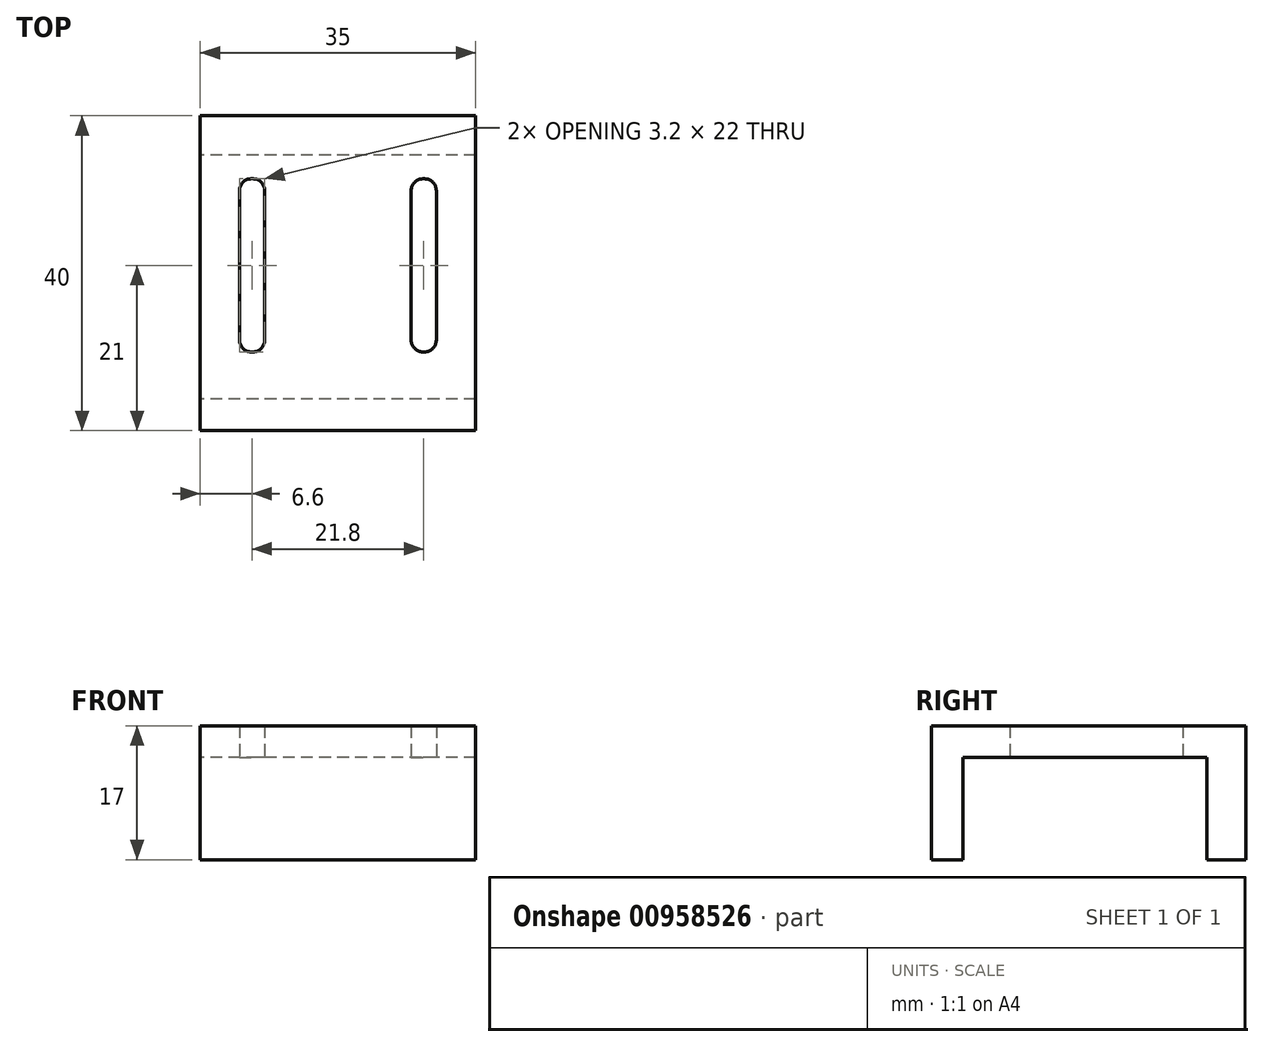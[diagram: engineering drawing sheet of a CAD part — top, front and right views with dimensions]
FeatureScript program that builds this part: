
annotation { "Feature Type Name" : "Feature", "Feature Type Description" : "" }
export const myFeature = defineFeature(function(context is Context, id is Id, definition is map)
    precondition{}
    {
        {
            var Q0;
            Q0=qCreatedBy(makeId("Top.planeOp"),FACE);
            var sketch = newSketch(context, id + "F0", { "sketchPlane" : qUnion([Q0])});
            skLineSegment(sketch, "E0.bottom", {"start": v(17.5, -20) * mm, "end": v(-17.5, -20) * mm});
            skLineSegment(sketch, "E0.top", {"start": v(17.5, 20) * mm, "end": v(-17.5, 20) * mm});
            skLineSegment(sketch, "E0.left", {"start": v(17.5, -20) * mm, "end": v(17.5, 20) * mm});
            skLineSegment(sketch, "E0.right", {"start": v(-17.5, -20) * mm, "end": v(-17.5, 20) * mm});
            skPoint(sketch, "E0.middle", {"position": v(0, 0) * mm});
            skLineSegment(sketch, "E1.bottom", {"start": v(-12.5, 12) * mm, "end": v(-9.3, 12) * mm});
            skLineSegment(sketch, "E1.top", {"start": v(-12.5, -10) * mm, "end": v(-9.3, -10) * mm});
            skLineSegment(sketch, "E1.left", {"start": v(-12.5, 12) * mm, "end": v(-12.5, -10) * mm});
            skLineSegment(sketch, "E1.right", {"start": v(-9.3, 12) * mm, "end": v(-9.3, -10) * mm});
            skLineSegment(sketch, "E2", {"start": v(0, 20) * mm, "end": v(0, -20) * mm, "construction": true});
            skLineSegment(sketch, "E3.1.0.0", {"start": v(9.3, 12) * mm, "end": v(12.5, 12) * mm});
            skLineSegment(sketch, "E3.1.0.1", {"start": v(12.5, 12) * mm, "end": v(12.5, -10) * mm});
            skLineSegment(sketch, "E3.1.0.2", {"start": v(9.3, 12) * mm, "end": v(9.3, -10) * mm});
            skLineSegment(sketch, "E3.1.0.3", {"start": v(9.3, -10) * mm, "end": v(12.5, -10) * mm});
            skLineSegment(sketch, "E3.direction1", {"start": v(-12.5, -10) * mm, "end": v(9.3, -10) * mm, "construction": true});
            skSolve(sketch);
        }
        {
            var Q0;
            Q0=makeQuery(id+"F0.imprint","IMPRINT",FACE,{"disambiguationData":[TD([[makeQuery(id+"F0.imprint","IMPRINT",EDGE,{"derivedFrom":sQuery(id+"F0.wireOp",EDGE,"E0.bottom")}),-1.0]])]});
            extrude(context, id + "F1", {"entities" : qUnion([Q0]), "depth" : 17 * mm, "offsetDistance" : 25 * mm});
        }
        {
            var Q0;
            Q0=makeQuery(id+"F1.opExtrude","SWEPT_FACE",FACE,{"disambiguationData":[OSD([sQuery(id+"F0.wireOp",EDGE,"E0.right")])]});
            var sketch = newSketch(context, id + "F2", { "sketchPlane" : qUnion([Q0])});
            skLineSegment(sketch, "E4.bottom", {"start": v(-15, 0) * mm, "end": v(16, 0) * mm});
            skLineSegment(sketch, "E4.top", {"start": v(-15, 13) * mm, "end": v(16, 13) * mm});
            skLineSegment(sketch, "E4.left", {"start": v(-15, 0) * mm, "end": v(-15, 13) * mm});
            skLineSegment(sketch, "E4.right", {"start": v(16, 0) * mm, "end": v(16, 13) * mm});
            skSolve(sketch);
        }
        {
            var Q0;
            Q0=makeQuery(id+"F2.imprint","IMPRINT",FACE,{"disambiguationData":[TD([[makeQuery(id+"F2.imprint","IMPRINT",EDGE,{"derivedFrom":sQuery(id+"F2.wireOp",EDGE,"E4.bottom")}),-1.0]])]});
            extrude(context, id + "F3", {"entities" : qUnion([Q0]), "operationType" : NewBodyOperationType.REMOVE, "endBound" : BoundingType.THROUGH_ALL, "oppositeDirection" : true, "depth" : 25 * mm, "offsetDistance" : 25 * mm});
        }
        {
            var Q0;
            Q0=makeQuery(id+"F1.opExtrude","SWEPT_EDGE",EDGE,{"disambiguationData":[OSD([sQuery(id+"F0.wireOp",EDGE,"E1.bottom"),sQuery(id+"F0.wireOp",EDGE,"E1.right")])]});
            var Q1;
            Q1=makeQuery(id+"F1.opExtrude","SWEPT_EDGE",EDGE,{"disambiguationData":[OSD([sQuery(id+"F0.wireOp",EDGE,"E1.bottom"),sQuery(id+"F0.wireOp",EDGE,"E1.left")])]});
            var Q2;
            Q2=makeQuery(id+"F1.opExtrude","SWEPT_EDGE",EDGE,{"disambiguationData":[OSD([sQuery(id+"F0.wireOp",EDGE,"E1.top"),sQuery(id+"F0.wireOp",EDGE,"E1.left")])]});
            var Q3;
            Q3=makeQuery(id+"F1.opExtrude","SWEPT_EDGE",EDGE,{"disambiguationData":[OSD([sQuery(id+"F0.wireOp",EDGE,"E1.top"),sQuery(id+"F0.wireOp",EDGE,"E1.right")])]});
            var Q4;
            Q4=makeQuery(id+"F1.opExtrude","SWEPT_EDGE",EDGE,{"disambiguationData":[OSD([sQuery(id+"F0.wireOp",EDGE,"E3.1.0.2"),sQuery(id+"F0.wireOp",EDGE,"E3.1.0.3")])]});
            var Q5;
            Q5=makeQuery(id+"F1.opExtrude","SWEPT_EDGE",EDGE,{"disambiguationData":[OSD([sQuery(id+"F0.wireOp",EDGE,"E3.1.0.1"),sQuery(id+"F0.wireOp",EDGE,"E3.1.0.3")])]});
            var Q6;
            Q6=makeQuery(id+"F1.opExtrude","SWEPT_EDGE",EDGE,{"disambiguationData":[OSD([sQuery(id+"F0.wireOp",EDGE,"E3.1.0.0"),sQuery(id+"F0.wireOp",EDGE,"E3.1.0.2")])]});
            var Q7;
            Q7=makeQuery(id+"F1.opExtrude","SWEPT_EDGE",EDGE,{"disambiguationData":[OSD([sQuery(id+"F0.wireOp",EDGE,"E3.1.0.0"),sQuery(id+"F0.wireOp",EDGE,"E3.1.0.1")])]});
            fillet(context, id + "F4", {"entities" : qUnion([Q0, Q1, Q2, Q3, Q4, Q5, Q6, Q7]), "radius" : 1.5 * mm, "tangentPropagation" : true, "allowEdgeOverflow" : false});
        }
    });
